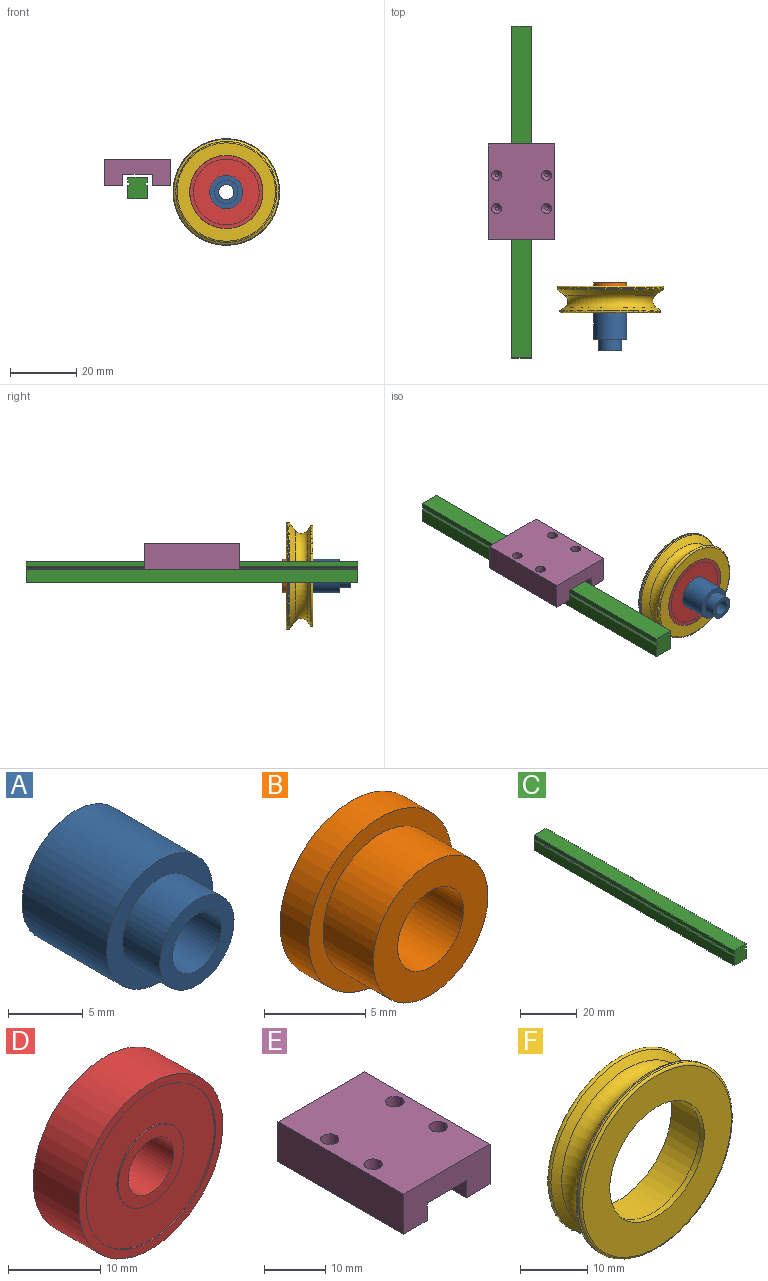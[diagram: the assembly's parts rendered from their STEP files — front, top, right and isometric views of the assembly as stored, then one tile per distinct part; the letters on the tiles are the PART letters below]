
ASSEMBLY  parts=6 mates=7
PART A: 6 faces, bbox 10x11.5x10 mm
  f0: cylinder r=5mm len=10mm, axis (0,-1,0), area 251.3mm2, adj f1,f2
  f1: plane 10x10mm, normal (0,1,0), area 61.9mm2, adj f0,f5
  f2: plane 10x10mm, normal (0,-1,0), area 40.1mm2, adj f0,f3
  f3: cylinder r=3.5mm len=7mm, axis (0,1,0), area 77mm2, adj f2,f4
  f4: plane 7x7mm, normal (0,-1,0), area 21.9mm2, adj f3,f5
  f5: cylinder r=2.3mm len=11.5mm, axis (0,-1,0), area 166.2mm2, adj f1,f4
PART B: 7 faces, bbox 10x5.5x10 mm
  f0: cylinder r=5mm len=10mm, axis (0,-1,0), area 62.8mm2, adj f1,f2
  f1: plane 10x10mm, normal (0,1,0), area 20.5mm2, adj f0,f6
  f2: plane 10x10mm, normal (0,-1,0), area 28.3mm2, adj f0,f3
  f3: cylinder r=4mm len=8mm, axis (0,1,0), area 88mm2, adj f2,f4
  f4: plane 8x8mm, normal (0,-1,0), area 33.6mm2, adj f3,f5
  f5: cylinder r=2.3mm len=4.6mm, axis (0,-1,0), area 50.6mm2, adj f4,f6
  f6: cone r=2.3mm half-angle=45deg, axis (0,1,0), area 58.6mm2, adj f1,f5
PART C: 12 faces, bbox 6x100x6.5 mm
  f0: plane 100x4mm, normal (-1,0,0), area 400mm2, adj f1,f9,f10,f11
  f1: plane 100x6mm, normal (0,0,-1), area 600mm2, adj f0,f2,f10,f11
  f2: plane 100x4mm, normal (1,0,0), area 400mm2, adj f1,f3,f10,f11
  f3: plane 100x0.5mm, normal (0.71,0,0.71), area 70.7mm2, adj f2,f4,f10,f11
  f4: plane 100x0.5mm, normal (0.71,0,-0.71), area 70.7mm2, adj f3,f5,f10,f11
  f5: plane 100x1.5mm, normal (1,0,0), area 150mm2, adj f4,f6,f10,f11
  f6: plane 100x6mm, normal (0,0,1), area 600mm2, adj f5,f7,f10,f11
  f7: plane 100x1.5mm, normal (-1,0,0), area 150mm2, adj f6,f8,f10,f11
  f8: plane 100x0.5mm, normal (-0.71,0,-0.71), area 70.7mm2, adj f7,f9,f10,f11
  f9: plane 100x0.5mm, normal (-0.71,0,0.71), area 70.7mm2, adj f0,f8,f10,f11
  f10: plane 6.5x6mm, normal (0,-1,0), area 38.5mm2, adj f0,f1,f2,f3,f4,f5,f6,f7
  f11: plane 6.5x6mm, normal (0,1,0), area 38.5mm2, adj f0,f1,f2,f3,f4,f5,f6,f7
PART D: 12 faces, bbox 22x7x22 mm
  f0: cylinder r=11mm len=22mm, axis (0,-1,0), area 483.8mm2, adj f1,f2
  f1: plane 22x22mm, normal (0,1,0), area 72.2mm2, adj f0,f8
  f2: plane 22x22mm, normal (0,-1,0), area 72.2mm2, adj f0,f4
  f3: cylinder r=5mm len=10mm, axis (0,-1,0), area 6.3mm2, adj f5,f6
  f4: cylinder r=9.9mm len=19.8mm, axis (0,-1,0), area 12.4mm2, adj f2,f5
  f5: plane 19.8x19.8mm, normal (0,-1,0), area 229.4mm2, adj f3,f4
  f6: plane 10x10mm, normal (0,-1,0), area 40.1mm2, adj f3,f11
  f7: cylinder r=5mm len=10mm, axis (0,1,0), area 6.3mm2, adj f9,f10
  f8: cylinder r=9.9mm len=19.8mm, axis (0,1,0), area 12.4mm2, adj f1,f9
  f9: plane 19.8x19.8mm, normal (0,1,0), area 229.4mm2, adj f7,f8
  f10: plane 10x10mm, normal (0,1,0), area 40.1mm2, adj f7,f11
  f11: cylinder r=3.5mm len=7mm, axis (0,-1,0), area 153.9mm2, adj f6,f10
PART E: 22 faces, bbox 20x28.9x8 mm
  f0: plane 28.9x5.5mm, normal (0,0,-1), area 158.9mm2, adj f1,f2,f4,f19
  f1: plane 28.9x8mm, normal (-1,0,0), area 231.2mm2, adj f0,f2,f4,f6
  f2: plane 20x8mm, normal (0,-1,0), area 128.5mm2, adj f0,f1,f3,f5,f6,f19,f20,f21
  f3: plane 28.9x8mm, normal (1,0,0), area 231.2mm2, adj f2,f4,f5,f6
  f4: plane 20x8mm, normal (0,1,0), area 128.5mm2, adj f0,f1,f3,f5,f6,f19,f20,f21
  f5: plane 28.9x5.5mm, normal (0,0,-1), area 158.9mm2, adj f2,f3,f4,f20
  f6: plane 28.9x20mm, normal (0,0,1), area 549.7mm2, adj f1,f2,f3,f4,f7,f9,f11,f13
  f7: cylinder r=1.5mm len=3mm, axis (0,0,1), area 18.8mm2, adj f6,f18
  f8: plane 1x1mm, normal (0,0,1), area 0.8mm2, adj f18
  f9: cylinder r=1.5mm len=3mm, axis (0,0,1), area 18.8mm2, adj f6,f15
  f10: plane 1x1mm, normal (0,0,1), area 0.8mm2, adj f15
  f11: cylinder r=1.5mm len=3mm, axis (0,0,1), area 18.8mm2, adj f6,f16
  f12: plane 1x1mm, normal (0,0,1), area 0.8mm2, adj f16
  f13: cylinder r=1.5mm len=3mm, axis (0,0,1), area 18.8mm2, adj f6,f17
  f14: plane 1x1mm, normal (0,0,1), area 0.8mm2, adj f17
  f15: cone r=0.5mm half-angle=45deg, axis (0,0,1), area 8.9mm2, adj f9,f10
  f16: cone r=0.5mm half-angle=45deg, axis (0,0,1), area 8.9mm2, adj f11,f12
  f17: cone r=0.5mm half-angle=45deg, axis (0,0,1), area 8.9mm2, adj f13,f14
  f18: cone r=0.5mm half-angle=45deg, axis (0,0,1), area 8.9mm2, adj f7,f8
  f19: plane 28.9x3.5mm, normal (1,0,0), area 101.1mm2, adj f0,f2,f4,f21
  f20: plane 28.9x3.5mm, normal (-1,0,0), area 101.1mm2, adj f2,f4,f5,f21
  f21: plane 28.9x9mm, normal (0,0,-1), area 260.1mm2, adj f2,f4,f19,f20
PART F: 12 faces, bbox 34.7x8x34.7 mm
  f0: plane 29.61x29.61mm, normal (0,1,0), area 305.2mm2, adj f8,f9
  f1: cone r=16.05mm half-angle=54.3deg, axis (0,1,0), area 145.9mm2, adj f2,f9
  f2: torus R=15.05mm, axis (0,1,0), area 352.6mm2, adj f1,f3
  f3: cone r=16.05mm half-angle=54.3deg, axis (0,-1,0), area 246.7mm2, adj f2,f10
  f4: cylinder r=16.05mm len=32.1mm, axis (0,1,0), area 39.8mm2, adj f10,f11
  f5: plane 31.3x31.3mm, normal (0,-1,0), area 458.4mm2, adj f6,f11
  f6: cylinder r=9.95mm len=19.9mm, axis (0,1,0), area 62.5mm2, adj f5,f7
  f7: plane 22.1x22.1mm, normal (0,1,0), area 72.6mm2, adj f6,f8
  f8: cylinder r=11.05mm len=22.1mm, axis (0,1,0), area 486mm2, adj f0,f7
  f9: torus R=14.81mm, axis (0,-1,0), area 95.6mm2, adj f0,f1
  f10: torus R=15.65mm, axis (0,-1,0), area 38.1mm2, adj f3,f4
  f11: torus R=15.65mm, axis (0,1,0), area 62.8mm2, adj f4,f5
PLACE A t=(35.8,-31.39,7.59)mm
PLACE B rot(axis=(0,-1,0),33.2deg) t=(35.8,-16.39,7.59)mm
PLACE C t=(6.07,62.99,5.5)mm
PLACE D rot(axis=(1,0,0),180deg) t=(35.8,-16.39,7.59)mm
PLACE E t=(-0.93,-1.46,17.5)mm
PLACE F rot(axis=(1,0,0),180deg) t=(35.8,-23.39,7.59)mm
MATE parallel C.f7 <-> E.f19  axis (-1,0,0) through (6.07,12.99,11.25)mm
MATE slider A.f0 <-> D.f11  axis (0,-1,0) through (35.8,-23.39,7.59)mm
MATE slider D.f0 <-> F.f1  axis (0,1,0) through (35.8,-19.89,7.59)mm
MATE planar D.f3 <-> A.f0  axis (0,-1,0) through (35.8,-23.39,7.59)mm
MATE planar D.f0 <-> F.f1  axis (0,1,0) through (35.8,-16.39,7.59)mm
MATE cylindrical B.f5 <-> D.f11  axis (0,-1,0) through (35.8,-18.14,7.59)mm
MATE planar D.f3 <-> B.f0  axis (0,1,0) through (35.8,-16.39,7.59)mm
